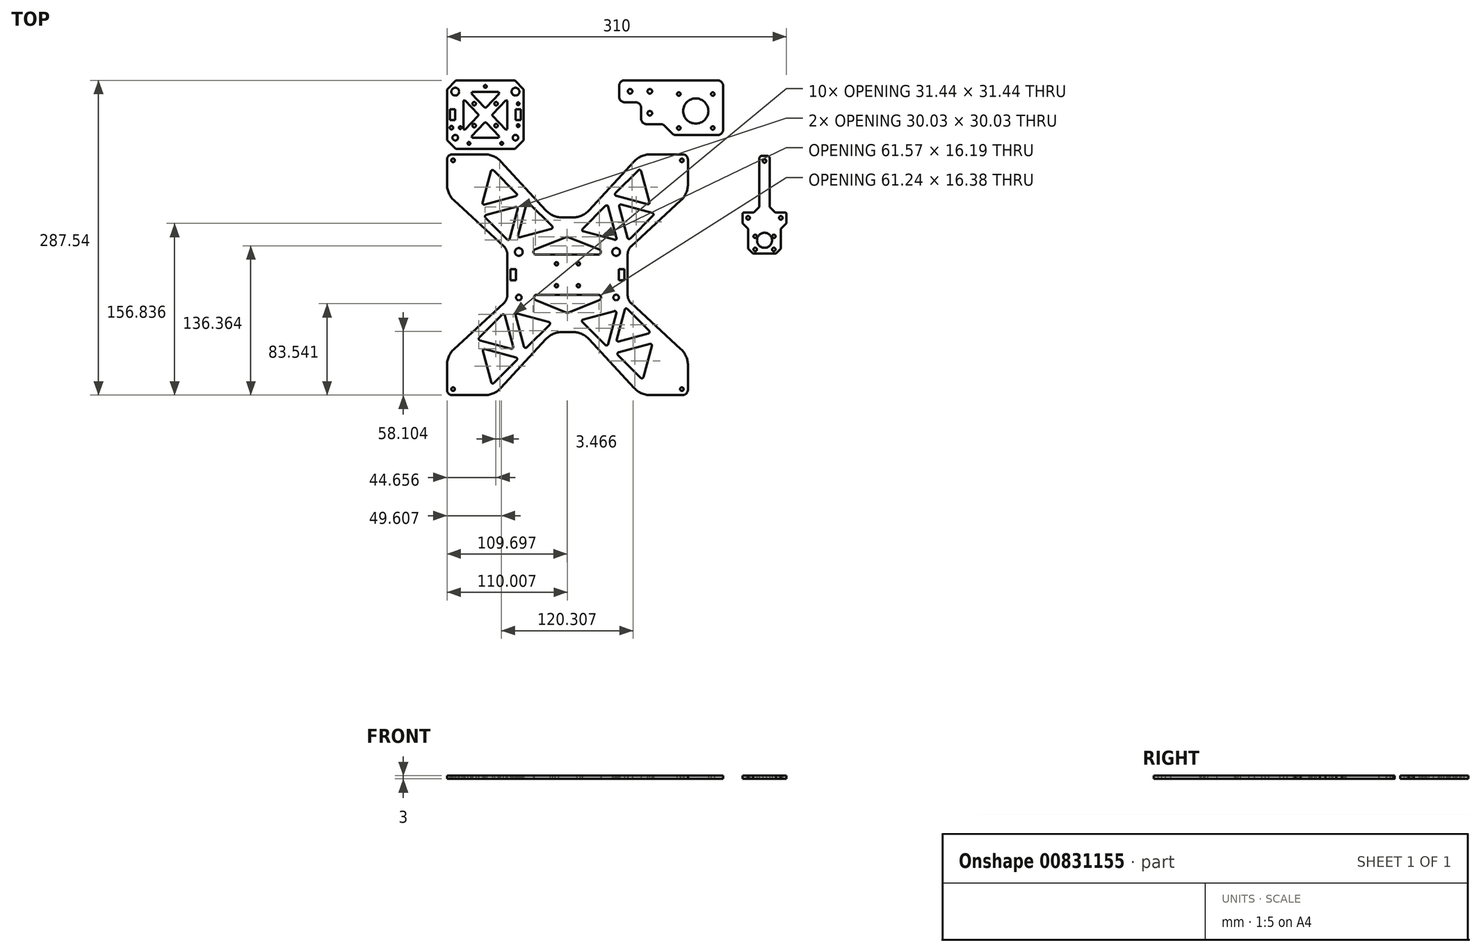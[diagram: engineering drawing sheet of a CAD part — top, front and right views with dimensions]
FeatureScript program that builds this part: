
annotation { "Feature Type Name" : "Feature", "Feature Type Description" : "" }
export const myFeature = defineFeature(function(context is Context, id is Id, definition is map)
    precondition{}
    {
        {
            var Q0;
            Q0=qCreatedBy(makeId("Top.planeOp"),FACE);
            var sketch = newSketch(context, id + "F0", { "sketchPlane" : qUnion([Q0])});
            skArc(sketch, "E0", {"start": v(205.4, 138.93) * mm, "mid": v(203.94, 142.47) * mm, "end": v(200.4, 143.93) * mm});
            skLineSegment(sketch, "E1", {"start": v(200.4, 143.93) * mm, "end": v(126.4, 143.93) * mm});
            skArc(sketch, "E2", {"start": v(126.4, 143.93) * mm, "mid": v(122.87, 142.47) * mm, "end": v(121.4, 138.93) * mm});
            skLineSegment(sketch, "E3", {"start": v(121.4, 138.93) * mm, "end": v(121.4, 107.13) * mm});
            skArc(sketch, "E4", {"start": v(121.4, 107.13) * mm, "mid": v(122.87, 103.6) * mm, "end": v(126.4, 102.13) * mm});
            skLineSegment(sketch, "E5", {"start": v(126.4, 102.13) * mm, "end": v(153.13, 102.13) * mm});
            skArc(sketch, "E6", {"start": v(156.67, 100.67) * mm, "mid": v(155.05, 101.75) * mm, "end": v(153.13, 102.13) * mm});
            skLineSegment(sketch, "E7", {"start": v(156.67, 100.67) * mm, "end": v(182.94, 74.4) * mm});
            skArc(sketch, "E8", {"start": v(184.4, 70.86) * mm, "mid": v(184.02, 72.78) * mm, "end": v(182.94, 74.4) * mm});
            skLineSegment(sketch, "E9", {"start": v(184.4, 70.86) * mm, "end": v(184.4, 46.93) * mm});
            skArc(sketch, "E10", {"start": v(184.4, 46.93) * mm, "mid": v(185.87, 43.4) * mm, "end": v(189.4, 41.93) * mm});
            skLineSegment(sketch, "E11", {"start": v(189.4, 41.93) * mm, "end": v(200.4, 41.93) * mm});
            skArc(sketch, "E12", {"start": v(200.4, 41.93) * mm, "mid": v(203.94, 43.4) * mm, "end": v(205.4, 46.93) * mm});
            skLineSegment(sketch, "E13", {"start": v(205.4, 46.93) * mm, "end": v(205.4, 138.93) * mm});
            skCircle(sketch, "E14", {"center": v(196.47, 51.76) * mm, "radius": 2.13 * mm});
            skCircle(sketch, "E15", {"center": v(196.47, 92.76) * mm, "radius": 2.13 * mm});
            skCircle(sketch, "E16", {"center": v(196.47, 134.1) * mm, "radius": 2.13 * mm});
            skArc(sketch, "E17", {"start": v(164.8, 136.93) * mm, "mid": v(166.4, 138.53) * mm, "end": v(164.8, 140.13) * mm});
            skLineSegment(sketch, "E18", {"start": v(164.8, 140.13) * mm, "end": v(158.8, 140.13) * mm});
            skArc(sketch, "E19", {"start": v(158.8, 140.13) * mm, "mid": v(157.2, 138.53) * mm, "end": v(158.8, 136.93) * mm});
            skLineSegment(sketch, "E20", {"start": v(158.8, 136.93) * mm, "end": v(164.8, 136.93) * mm});
            skArc(sketch, "E21", {"start": v(133.8, 105.93) * mm, "mid": v(135.4, 107.53) * mm, "end": v(133.8, 109.13) * mm});
            skLineSegment(sketch, "E22", {"start": v(133.8, 109.13) * mm, "end": v(127.8, 109.13) * mm});
            skArc(sketch, "E23", {"start": v(127.8, 109.13) * mm, "mid": v(126.2, 107.53) * mm, "end": v(127.8, 105.93) * mm});
            skLineSegment(sketch, "E24", {"start": v(127.8, 105.93) * mm, "end": v(133.8, 105.93) * mm});
            skArc(sketch, "E25", {"start": v(127.8, 140.13) * mm, "mid": v(126.2, 138.53) * mm, "end": v(127.8, 136.93) * mm});
            skLineSegment(sketch, "E26", {"start": v(127.8, 136.93) * mm, "end": v(133.8, 136.93) * mm});
            skArc(sketch, "E27", {"start": v(133.8, 136.93) * mm, "mid": v(135.4, 138.53) * mm, "end": v(133.8, 140.13) * mm});
            skLineSegment(sketch, "E28", {"start": v(133.8, 140.13) * mm, "end": v(127.8, 140.13) * mm});
            skLineSegment(sketch, "E29", {"start": v(149.1, 134.53) * mm, "end": v(143.1, 134.53) * mm});
            skArc(sketch, "E30", {"start": v(143.1, 134.53) * mm, "mid": v(131.6, 123.03) * mm, "end": v(143.1, 111.53) * mm});
            skLineSegment(sketch, "E31", {"start": v(143.1, 111.53) * mm, "end": v(149.1, 111.53) * mm});
            skArc(sketch, "E32", {"start": v(149.1, 111.53) * mm, "mid": v(160.6, 123.03) * mm, "end": v(149.1, 134.53) * mm});
            skArc(sketch, "E33", {"start": v(164.8, 105.93) * mm, "mid": v(166.4, 107.53) * mm, "end": v(164.8, 109.13) * mm});
            skLineSegment(sketch, "E34", {"start": v(164.8, 109.13) * mm, "end": v(158.8, 109.13) * mm});
            skArc(sketch, "E35", {"start": v(158.8, 109.13) * mm, "mid": v(157.2, 107.53) * mm, "end": v(158.8, 105.93) * mm});
            skLineSegment(sketch, "E36", {"start": v(158.8, 105.93) * mm, "end": v(164.8, 105.93) * mm});
            skLineSegment(sketch, "E37", {"start": v(205.25, -63.38) * mm, "end": v(205.25, -1.88) * mm});
            skArc(sketch, "E38", {"start": v(205.25, -1.88) * mm, "mid": v(204.37, 0.24) * mm, "end": v(202.25, 1.12) * mm});
            skLineSegment(sketch, "E39", {"start": v(202.25, 1.12) * mm, "end": v(168.25, 1.12) * mm});
            skArc(sketch, "E40", {"start": v(168.25, 1.12) * mm, "mid": v(166.12, 0.24) * mm, "end": v(165.25, -1.88) * mm});
            skLineSegment(sketch, "E41", {"start": v(165.25, -1.88) * mm, "end": v(165.25, -43.38) * mm});
            skArc(sketch, "E42", {"start": v(162.25, -46.38) * mm, "mid": v(164.37, -45.5) * mm, "end": v(165.25, -43.38) * mm});
            skLineSegment(sketch, "E43", {"start": v(162.25, -46.38) * mm, "end": v(120.75, -46.28) * mm});
            skArc(sketch, "E44", {"start": v(120.75, -46.28) * mm, "mid": v(118.63, -47.16) * mm, "end": v(117.75, -49.28) * mm});
            skLineSegment(sketch, "E45", {"start": v(117.75, -49.28) * mm, "end": v(117.75, -63.38) * mm});
            skArc(sketch, "E46", {"start": v(117.75, -63.38) * mm, "mid": v(118.62, -65.5) * mm, "end": v(120.75, -66.38) * mm});
            skLineSegment(sketch, "E47", {"start": v(120.75, -66.38) * mm, "end": v(202.25, -66.38) * mm});
            skArc(sketch, "E48", {"start": v(202.25, -66.38) * mm, "mid": v(204.37, -65.5) * mm, "end": v(205.25, -63.38) * mm});
            skCircle(sketch, "E49", {"center": v(195.25, -28.88) * mm, "radius": 2.15 * mm});
            skCircle(sketch, "E50", {"center": v(175.25, -28.88) * mm, "radius": 2.15 * mm});
            skCircle(sketch, "E51", {"center": v(195.25, -8.88) * mm, "radius": 2.15 * mm});
            skCircle(sketch, "E52", {"center": v(127.75, -56.33) * mm, "radius": 2.15 * mm});
            skCircle(sketch, "E53", {"center": v(147.75, -56.33) * mm, "radius": 2.15 * mm});
            skCircle(sketch, "E54", {"center": v(175.25, -8.88) * mm, "radius": 2.15 * mm});
            skLineSegment(sketch, "E55", {"start": v(117.74, -126.84) * mm, "end": v(117.74, -140.93) * mm});
            skArc(sketch, "E56", {"start": v(117.74, -140.93) * mm, "mid": v(118.62, -143.05) * mm, "end": v(120.74, -143.93) * mm});
            skLineSegment(sketch, "E57", {"start": v(120.74, -143.93) * mm, "end": v(202.24, -143.93) * mm});
            skArc(sketch, "E58", {"start": v(202.24, -143.93) * mm, "mid": v(204.37, -143.05) * mm, "end": v(205.24, -140.93) * mm});
            skLineSegment(sketch, "E59", {"start": v(205.24, -140.93) * mm, "end": v(205.24, -79.43) * mm});
            skArc(sketch, "E60", {"start": v(205.24, -79.43) * mm, "mid": v(204.37, -77.31) * mm, "end": v(202.24, -76.43) * mm});
            skLineSegment(sketch, "E61", {"start": v(202.24, -76.43) * mm, "end": v(168.24, -76.43) * mm});
            skArc(sketch, "E62", {"start": v(168.24, -76.43) * mm, "mid": v(166.12, -77.31) * mm, "end": v(165.24, -79.43) * mm});
            skLineSegment(sketch, "E63", {"start": v(165.24, -79.43) * mm, "end": v(165.24, -120.93) * mm});
            skArc(sketch, "E64", {"start": v(162.24, -123.93) * mm, "mid": v(164.37, -123.05) * mm, "end": v(165.24, -120.93) * mm});
            skLineSegment(sketch, "E65", {"start": v(162.24, -123.93) * mm, "end": v(120.75, -123.84) * mm});
            skArc(sketch, "E66", {"start": v(120.75, -123.84) * mm, "mid": v(118.63, -124.71) * mm, "end": v(117.74, -126.84) * mm});
            skCircle(sketch, "E67", {"center": v(127.74, -133.89) * mm, "radius": 2.15 * mm});
            skCircle(sketch, "E68", {"center": v(147.74, -133.89) * mm, "radius": 2.15 * mm});
            skCircle(sketch, "E69", {"center": v(175.24, -106.43) * mm, "radius": 2.15 * mm});
            skCircle(sketch, "E70", {"center": v(195.24, -106.43) * mm, "radius": 2.15 * mm});
            skCircle(sketch, "E71", {"center": v(175.24, -86.43) * mm, "radius": 2.15 * mm});
            skCircle(sketch, "E72", {"center": v(195.24, -86.43) * mm, "radius": 2.15 * mm});
            skLineSegment(sketch, "E73", {"start": v(134.6, 23.18) * mm, "end": v(134.6, -38.32) * mm});
            skArc(sketch, "E74", {"start": v(134.6, -38.32) * mm, "mid": v(135.47, -40.44) * mm, "end": v(137.6, -41.32) * mm});
            skLineSegment(sketch, "E75", {"start": v(137.6, -41.32) * mm, "end": v(151.6, -41.32) * mm});
            skArc(sketch, "E76", {"start": v(151.6, -41.32) * mm, "mid": v(153.72, -40.44) * mm, "end": v(154.6, -38.32) * mm});
            skLineSegment(sketch, "E77", {"start": v(154.6, -38.32) * mm, "end": v(154.6, 3.18) * mm});
            skArc(sketch, "E78", {"start": v(157.6, 6.18) * mm, "mid": v(155.47, 5.3) * mm, "end": v(154.6, 3.18) * mm});
            skLineSegment(sketch, "E79", {"start": v(157.6, 6.18) * mm, "end": v(199.1, 6.18) * mm});
            skArc(sketch, "E80", {"start": v(199.1, 6.18) * mm, "mid": v(201.22, 7.06) * mm, "end": v(202.1, 9.18) * mm});
            skLineSegment(sketch, "E81", {"start": v(202.1, 9.18) * mm, "end": v(202.1, 23.18) * mm});
            skArc(sketch, "E82", {"start": v(202.1, 23.18) * mm, "mid": v(201.22, 25.3) * mm, "end": v(199.1, 26.18) * mm});
            skLineSegment(sketch, "E83", {"start": v(199.1, 26.18) * mm, "end": v(137.6, 26.18) * mm});
            skArc(sketch, "E84", {"start": v(137.6, 26.18) * mm, "mid": v(135.47, 25.3) * mm, "end": v(134.6, 23.18) * mm});
            skCircle(sketch, "E85", {"center": v(144.6, -31.32) * mm, "radius": 2.15 * mm});
            skCircle(sketch, "E86", {"center": v(192.1, 16.18) * mm, "radius": 2.15 * mm});
            skCircle(sketch, "E87", {"center": v(172.1, 16.18) * mm, "radius": 2.15 * mm});
            skCircle(sketch, "E88", {"center": v(144.6, -11.32) * mm, "radius": 2.15 * mm});
            skArc(sketch, "E89", {"start": v(94.35, 38.03) * mm, "mid": v(95.81, 34.5) * mm, "end": v(99.35, 33.03) * mm});
            skLineSegment(sketch, "E90", {"start": v(99.35, 33.03) * mm, "end": v(173.35, 33.03) * mm});
            skArc(sketch, "E91", {"start": v(173.35, 33.03) * mm, "mid": v(176.88, 34.5) * mm, "end": v(178.35, 38.03) * mm});
            skLineSegment(sketch, "E92", {"start": v(178.35, 38.03) * mm, "end": v(178.35, 69.83) * mm});
            skArc(sketch, "E93", {"start": v(178.35, 69.83) * mm, "mid": v(176.88, 73.37) * mm, "end": v(173.35, 74.83) * mm});
            skLineSegment(sketch, "E94", {"start": v(173.35, 74.83) * mm, "end": v(146.62, 74.83) * mm});
            skArc(sketch, "E95", {"start": v(143.08, 76.3) * mm, "mid": v(144.7, 75.21) * mm, "end": v(146.62, 74.83) * mm});
            skLineSegment(sketch, "E96", {"start": v(143.08, 76.3) * mm, "end": v(116.8, 102.57) * mm});
            skArc(sketch, "E97", {"start": v(115.35, 106.1) * mm, "mid": v(115.73, 104.19) * mm, "end": v(116.8, 102.57) * mm});
            skLineSegment(sketch, "E98", {"start": v(115.35, 106.1) * mm, "end": v(115.35, 130.03) * mm});
            skArc(sketch, "E99", {"start": v(115.35, 130.03) * mm, "mid": v(113.88, 133.57) * mm, "end": v(110.35, 135.03) * mm});
            skLineSegment(sketch, "E100", {"start": v(110.35, 135.03) * mm, "end": v(99.35, 135.03) * mm});
            skArc(sketch, "E101", {"start": v(99.35, 135.03) * mm, "mid": v(95.81, 133.57) * mm, "end": v(94.35, 130.03) * mm});
            skLineSegment(sketch, "E102", {"start": v(94.35, 130.03) * mm, "end": v(94.35, 38.03) * mm});
            skCircle(sketch, "E103", {"center": v(103.28, 125.2) * mm, "radius": 2.13 * mm});
            skCircle(sketch, "E104", {"center": v(103.28, 84.2) * mm, "radius": 2.13 * mm});
            skCircle(sketch, "E105", {"center": v(103.28, 42.86) * mm, "radius": 2.13 * mm});
            skArc(sketch, "E106", {"start": v(165.95, 71.03) * mm, "mid": v(164.35, 69.43) * mm, "end": v(165.95, 67.83) * mm});
            skLineSegment(sketch, "E107", {"start": v(165.95, 67.83) * mm, "end": v(171.95, 67.83) * mm});
            skArc(sketch, "E108", {"start": v(171.95, 67.83) * mm, "mid": v(173.55, 69.43) * mm, "end": v(171.95, 71.03) * mm});
            skLineSegment(sketch, "E109", {"start": v(171.95, 71.03) * mm, "end": v(165.95, 71.03) * mm});
            skArc(sketch, "E110", {"start": v(171.95, 36.83) * mm, "mid": v(173.55, 38.43) * mm, "end": v(171.95, 40.03) * mm});
            skLineSegment(sketch, "E111", {"start": v(171.95, 40.03) * mm, "end": v(165.95, 40.03) * mm});
            skArc(sketch, "E112", {"start": v(165.95, 40.03) * mm, "mid": v(164.35, 38.43) * mm, "end": v(165.95, 36.83) * mm});
            skLineSegment(sketch, "E113", {"start": v(165.95, 36.83) * mm, "end": v(171.95, 36.83) * mm});
            skLineSegment(sketch, "E114", {"start": v(150.65, 42.43) * mm, "end": v(156.65, 42.43) * mm});
            skArc(sketch, "E115", {"start": v(156.65, 42.43) * mm, "mid": v(168.15, 53.93) * mm, "end": v(156.65, 65.43) * mm});
            skLineSegment(sketch, "E116", {"start": v(156.65, 65.43) * mm, "end": v(150.65, 65.43) * mm});
            skArc(sketch, "E117", {"start": v(150.65, 65.43) * mm, "mid": v(139.15, 53.93) * mm, "end": v(150.65, 42.43) * mm});
            skArc(sketch, "E118", {"start": v(134.95, 40.03) * mm, "mid": v(133.35, 38.43) * mm, "end": v(134.95, 36.83) * mm});
            skLineSegment(sketch, "E119", {"start": v(134.95, 36.83) * mm, "end": v(140.95, 36.83) * mm});
            skArc(sketch, "E120", {"start": v(140.95, 36.83) * mm, "mid": v(142.55, 38.43) * mm, "end": v(140.95, 40.03) * mm});
            skLineSegment(sketch, "E121", {"start": v(140.95, 40.03) * mm, "end": v(134.95, 40.03) * mm});
            skArc(sketch, "E122", {"start": v(134.95, 71.03) * mm, "mid": v(133.35, 69.43) * mm, "end": v(134.95, 67.83) * mm});
            skLineSegment(sketch, "E123", {"start": v(134.95, 67.83) * mm, "end": v(140.95, 67.83) * mm});
            skArc(sketch, "E124", {"start": v(140.95, 67.83) * mm, "mid": v(142.55, 69.43) * mm, "end": v(140.95, 71.03) * mm});
            skLineSegment(sketch, "E125", {"start": v(140.95, 71.03) * mm, "end": v(134.95, 71.03) * mm});
            skLineSegment(sketch, "E126", {"start": v(59.22, -44.47) * mm, "end": v(27.33, -44.47) * mm});
            skArc(sketch, "E127", {"start": v(27.33, -44.47) * mm, "mid": v(23.8, -45.93) * mm, "end": v(22.33, -49.47) * mm});
            skLineSegment(sketch, "E128", {"start": v(22.33, -49.47) * mm, "end": v(22.33, -138.36) * mm});
            skArc(sketch, "E129", {"start": v(22.33, -138.36) * mm, "mid": v(23.8, -141.9) * mm, "end": v(27.33, -143.36) * mm});
            skLineSegment(sketch, "E130", {"start": v(27.33, -143.36) * mm, "end": v(99.71, -143.36) * mm});
            skArc(sketch, "E131", {"start": v(99.71, -143.36) * mm, "mid": v(103.25, -141.9) * mm, "end": v(104.71, -138.36) * mm});
            skLineSegment(sketch, "E132", {"start": v(104.71, -138.36) * mm, "end": v(104.71, -134.17) * mm});
            skArc(sketch, "E133", {"start": v(106.57, -129.68) * mm, "mid": v(105.2, -131.74) * mm, "end": v(104.71, -134.17) * mm});
            skLineSegment(sketch, "E134", {"start": v(106.57, -129.68) * mm, "end": v(115.55, -120.7) * mm});
            skArc(sketch, "E135", {"start": v(120.04, -118.84) * mm, "mid": v(117.61, -119.32) * mm, "end": v(115.55, -120.7) * mm});
            skLineSegment(sketch, "E136", {"start": v(120.04, -118.84) * mm, "end": v(149.78, -118.84) * mm});
            skArc(sketch, "E137", {"start": v(149.78, -118.84) * mm, "mid": v(153.32, -117.37) * mm, "end": v(154.78, -113.84) * mm});
            skLineSegment(sketch, "E138", {"start": v(154.78, -113.84) * mm, "end": v(154.78, -76.38) * mm});
            skArc(sketch, "E139", {"start": v(154.78, -76.38) * mm, "mid": v(153.32, -72.84) * mm, "end": v(149.78, -71.38) * mm});
            skLineSegment(sketch, "E140", {"start": v(149.78, -71.38) * mm, "end": v(120.04, -71.38) * mm});
            skArc(sketch, "E141", {"start": v(115.55, -69.52) * mm, "mid": v(117.61, -70.9) * mm, "end": v(120.04, -71.38) * mm});
            skLineSegment(sketch, "E142", {"start": v(115.55, -69.52) * mm, "end": v(106.57, -60.54) * mm});
            skArc(sketch, "E143", {"start": v(104.71, -56.05) * mm, "mid": v(105.2, -58.48) * mm, "end": v(106.57, -60.54) * mm});
            skLineSegment(sketch, "E144", {"start": v(104.71, -56.05) * mm, "end": v(104.71, -49.47) * mm});
            skArc(sketch, "E145", {"start": v(104.71, -49.47) * mm, "mid": v(103.25, -45.93) * mm, "end": v(99.71, -44.47) * mm});
            skLineSegment(sketch, "E146", {"start": v(99.71, -44.47) * mm, "end": v(67.83, -44.47) * mm});
            skArc(sketch, "E147", {"start": v(67.83, -44.47) * mm, "mid": v(67.06, -44.62) * mm, "end": v(66.42, -45.06) * mm});
            skLineSegment(sketch, "E148", {"start": v(66.42, -45.06) * mm, "end": v(64.94, -46.53) * mm});
            skArc(sketch, "E149", {"start": v(62.1, -46.53) * mm, "mid": v(63.52, -47.12) * mm, "end": v(64.94, -46.53) * mm});
            skLineSegment(sketch, "E150", {"start": v(62.1, -46.53) * mm, "end": v(60.63, -45.06) * mm});
            skArc(sketch, "E151", {"start": v(60.63, -45.06) * mm, "mid": v(59.98, -44.62) * mm, "end": v(59.22, -44.47) * mm});
            skCircle(sketch, "E152", {"center": v(94.46, -54.47) * mm, "radius": 3.56 * mm});
            skCircle(sketch, "E153", {"center": v(94.46, -133.36) * mm, "radius": 3.56 * mm});
            skCircle(sketch, "E154", {"center": v(32.59, -54.47) * mm, "radius": 2.55 * mm});
            skCircle(sketch, "E155", {"center": v(32.59, -133.36) * mm, "radius": 2.55 * mm});
            skCircle(sketch, "E156", {"center": v(89.52, -98.83) * mm, "radius": 2.1 * mm});
            skCircle(sketch, "E157", {"center": v(37.52, -98.83) * mm, "radius": 2.1 * mm});
            skCircle(sketch, "E158", {"center": v(89.52, -78.83) * mm, "radius": 2.1 * mm});
            skCircle(sketch, "E159", {"center": v(37.52, -78.83) * mm, "radius": 2.1 * mm});
            skCircle(sketch, "E160", {"center": v(145.28, -111.34) * mm, "radius": 1.6 * mm});
            skCircle(sketch, "E161", {"center": v(129.78, -95.84) * mm, "radius": 11.5 * mm});
            skCircle(sketch, "E162", {"center": v(145.28, -80.34) * mm, "radius": 1.6 * mm});
            skCircle(sketch, "E163", {"center": v(114.28, -111.34) * mm, "radius": 1.6 * mm});
            skCircle(sketch, "E164", {"center": v(114.28, -80.34) * mm, "radius": 1.6 * mm});
            skArc(sketch, "E165", {"start": v(47.67, -58.84) * mm, "mid": v(44.84, -60.01) * mm, "end": v(43.67, -62.84) * mm});
            skLineSegment(sketch, "E166", {"start": v(43.67, -62.84) * mm, "end": v(43.67, -123.72) * mm});
            skArc(sketch, "E167", {"start": v(43.67, -123.72) * mm, "mid": v(44.84, -126.54) * mm, "end": v(47.67, -127.72) * mm});
            skLineSegment(sketch, "E168", {"start": v(47.67, -127.72) * mm, "end": v(79.38, -127.72) * mm});
            skArc(sketch, "E169", {"start": v(79.38, -127.72) * mm, "mid": v(82.2, -126.54) * mm, "end": v(83.38, -123.72) * mm});
            skLineSegment(sketch, "E170", {"start": v(83.38, -123.72) * mm, "end": v(83.38, -62.84) * mm});
            skArc(sketch, "E171", {"start": v(83.38, -62.84) * mm, "mid": v(82.2, -60.01) * mm, "end": v(79.38, -58.84) * mm});
            skLineSegment(sketch, "E172", {"start": v(79.38, -58.84) * mm, "end": v(47.67, -58.84) * mm});
            skLineSegment(sketch, "E173", {"start": v(62.1, -22.47) * mm, "end": v(62.1, -36.47) * mm});
            skArc(sketch, "E174", {"start": v(62.1, -36.47) * mm, "mid": v(62.97, -38.6) * mm, "end": v(65.1, -39.47) * mm});
            skLineSegment(sketch, "E175", {"start": v(65.1, -39.47) * mm, "end": v(126.6, -39.47) * mm});
            skArc(sketch, "E176", {"start": v(126.6, -39.47) * mm, "mid": v(128.72, -38.6) * mm, "end": v(129.6, -36.47) * mm});
            skLineSegment(sketch, "E177", {"start": v(129.6, -36.47) * mm, "end": v(129.6, 25.03) * mm});
            skArc(sketch, "E178", {"start": v(129.6, 25.03) * mm, "mid": v(128.72, 27.15) * mm, "end": v(126.6, 28.03) * mm});
            skLineSegment(sketch, "E179", {"start": v(126.6, 28.03) * mm, "end": v(112.6, 28.03) * mm});
            skArc(sketch, "E180", {"start": v(112.6, 28.03) * mm, "mid": v(110.47, 27.15) * mm, "end": v(109.6, 25.03) * mm});
            skLineSegment(sketch, "E181", {"start": v(109.6, 25.03) * mm, "end": v(109.6, -16.47) * mm});
            skArc(sketch, "E182", {"start": v(106.6, -19.47) * mm, "mid": v(108.72, -18.6) * mm, "end": v(109.6, -16.47) * mm});
            skLineSegment(sketch, "E183", {"start": v(106.6, -19.47) * mm, "end": v(65.1, -19.47) * mm});
            skArc(sketch, "E184", {"start": v(65.1, -19.47) * mm, "mid": v(62.97, -20.35) * mm, "end": v(62.1, -22.47) * mm});
            skCircle(sketch, "E185", {"center": v(72.1, -29.47) * mm, "radius": 2.15 * mm});
            skCircle(sketch, "E186", {"center": v(92.1, -29.47) * mm, "radius": 2.15 * mm});
            skCircle(sketch, "E187", {"center": v(119.6, 18.03) * mm, "radius": 2.15 * mm});
            skCircle(sketch, "E188", {"center": v(119.6, -1.97) * mm, "radius": 2.15 * mm});
            skLineSegment(sketch, "E189", {"start": v(79.85, 72.21) * mm, "end": v(79.85, 28.05) * mm});
            skLineSegment(sketch, "E190", {"start": v(79.85, 28.05) * mm, "end": v(74.77, 22.97) * mm});
            skLineSegment(sketch, "E191", {"start": v(74.77, 22.97) * mm, "end": v(65.87, 22.97) * mm});
            skArc(sketch, "E192", {"start": v(65.87, 22.97) * mm, "mid": v(64.97, 22.6) * mm, "end": v(64.6, 21.7) * mm});
            skLineSegment(sketch, "E193", {"start": v(64.6, 21.7) * mm, "end": v(64.6, 13.03) * mm});
            skLineSegment(sketch, "E194", {"start": v(64.6, 13.03) * mm, "end": v(69.6, 8.03) * mm});
            skLineSegment(sketch, "E195", {"start": v(69.6, 8.03) * mm, "end": v(69.6, -9.97) * mm});
            skLineSegment(sketch, "E196", {"start": v(69.6, -9.97) * mm, "end": v(74.1, -14.47) * mm});
            skLineSegment(sketch, "E197", {"start": v(74.1, -14.47) * mm, "end": v(95.1, -14.47) * mm});
            skLineSegment(sketch, "E198", {"start": v(95.1, -14.47) * mm, "end": v(99.6, -9.97) * mm});
            skLineSegment(sketch, "E199", {"start": v(99.6, -9.97) * mm, "end": v(99.6, 8.03) * mm});
            skLineSegment(sketch, "E200", {"start": v(99.6, 8.03) * mm, "end": v(104.6, 13.03) * mm});
            skLineSegment(sketch, "E201", {"start": v(104.6, 13.03) * mm, "end": v(104.6, 21.7) * mm});
            skArc(sketch, "E202", {"start": v(104.6, 21.7) * mm, "mid": v(104.22, 22.6) * mm, "end": v(103.33, 22.97) * mm});
            skLineSegment(sketch, "E203", {"start": v(103.33, 22.97) * mm, "end": v(94.43, 22.97) * mm});
            skLineSegment(sketch, "E204", {"start": v(94.43, 22.97) * mm, "end": v(89.35, 28.05) * mm});
            skLineSegment(sketch, "E205", {"start": v(89.35, 28.05) * mm, "end": v(89.35, 72.21) * mm});
            skArc(sketch, "E206", {"start": v(89.35, 72.21) * mm, "mid": v(88.6, 74) * mm, "end": v(86.8, 74.75) * mm});
            skLineSegment(sketch, "E207", {"start": v(86.8, 74.75) * mm, "end": v(82.39, 74.75) * mm});
            skArc(sketch, "E208", {"start": v(82.39, 74.75) * mm, "mid": v(80.6, 74) * mm, "end": v(79.85, 72.21) * mm});
            skCircle(sketch, "E209", {"center": v(84.6, -2.47) * mm, "radius": 6.88 * mm});
            skCircle(sketch, "E210", {"center": v(76.1, 1.13) * mm, "radius": 1.59 * mm});
            skCircle(sketch, "E211", {"center": v(93.1, 1.13) * mm, "radius": 1.59 * mm});
            skCircle(sketch, "E212", {"center": v(76.1, -10.87) * mm, "radius": 1.59 * mm});
            skCircle(sketch, "E213", {"center": v(93.1, -10.87) * mm, "radius": 1.59 * mm});
            skCircle(sketch, "E214", {"center": v(84.6, 69.99) * mm, "radius": 1.64 * mm});
            skCircle(sketch, "E215", {"center": v(99.51, 18) * mm, "radius": 1.64 * mm});
            skCircle(sketch, "E216", {"center": v(69.57, 18) * mm, "radius": 1.64 * mm});
            skLineSegment(sketch, "E217", {"start": v(74.1, 32.84) * mm, "end": v(74.1, 77) * mm});
            skLineSegment(sketch, "E218", {"start": v(74.1, 77) * mm, "end": v(79.18, 82.08) * mm});
            skLineSegment(sketch, "E219", {"start": v(79.18, 82.08) * mm, "end": v(88.08, 82.08) * mm});
            skArc(sketch, "E220", {"start": v(88.08, 82.08) * mm, "mid": v(88.97, 82.45) * mm, "end": v(89.35, 83.35) * mm});
            skLineSegment(sketch, "E221", {"start": v(89.35, 83.35) * mm, "end": v(89.35, 92.02) * mm});
            skLineSegment(sketch, "E222", {"start": v(89.35, 92.02) * mm, "end": v(84.35, 97.02) * mm});
            skLineSegment(sketch, "E223", {"start": v(84.35, 97.02) * mm, "end": v(84.35, 116.52) * mm});
            skLineSegment(sketch, "E224", {"start": v(84.35, 116.52) * mm, "end": v(76.35, 124.52) * mm});
            skLineSegment(sketch, "E225", {"start": v(76.35, 124.52) * mm, "end": v(62.35, 124.52) * mm});
            skLineSegment(sketch, "E226", {"start": v(62.35, 124.52) * mm, "end": v(54.35, 116.52) * mm});
            skLineSegment(sketch, "E227", {"start": v(54.35, 116.52) * mm, "end": v(54.35, 97.02) * mm});
            skLineSegment(sketch, "E228", {"start": v(54.35, 97.02) * mm, "end": v(49.35, 92.02) * mm});
            skLineSegment(sketch, "E229", {"start": v(49.35, 92.02) * mm, "end": v(49.35, 83.35) * mm});
            skArc(sketch, "E230", {"start": v(49.35, 83.35) * mm, "mid": v(49.72, 82.45) * mm, "end": v(50.62, 82.08) * mm});
            skLineSegment(sketch, "E231", {"start": v(50.62, 82.08) * mm, "end": v(59.52, 82.08) * mm});
            skLineSegment(sketch, "E232", {"start": v(59.52, 82.08) * mm, "end": v(64.6, 77) * mm});
            skLineSegment(sketch, "E233", {"start": v(64.6, 77) * mm, "end": v(64.6, 32.84) * mm});
            skArc(sketch, "E234", {"start": v(64.6, 32.84) * mm, "mid": v(65.34, 31.04) * mm, "end": v(67.14, 30.3) * mm});
            skLineSegment(sketch, "E235", {"start": v(67.14, 30.3) * mm, "end": v(71.56, 30.3) * mm});
            skArc(sketch, "E236", {"start": v(71.56, 30.3) * mm, "mid": v(73.35, 31.04) * mm, "end": v(74.1, 32.84) * mm});
            skCircle(sketch, "E237", {"center": v(69.35, 120.08) * mm, "radius": 1.24 * mm});
            skCircle(sketch, "E238", {"center": v(74.35, 95.02) * mm, "radius": 1.6 * mm});
            skCircle(sketch, "E239", {"center": v(69.35, 107.52) * mm, "radius": 8.1 * mm});
            skCircle(sketch, "E240", {"center": v(64.35, 94.98) * mm, "radius": 1.6 * mm});
            skCircle(sketch, "E241", {"center": v(69.35, 35.06) * mm, "radius": 1.64 * mm});
            skCircle(sketch, "E242", {"center": v(84.38, 87.05) * mm, "radius": 1.64 * mm});
            skCircle(sketch, "E243", {"center": v(54.43, 87.05) * mm, "radius": 1.64 * mm});
            skLineSegment(sketch, "E244", {"start": v(48.67, -111.25) * mm, "end": v(48.67, -119.28) * mm});
            skArc(sketch, "E245", {"start": v(48.67, -119.28) * mm, "mid": v(48.72, -119.52) * mm, "end": v(48.85, -119.73) * mm});
            skLineSegment(sketch, "E246", {"start": v(48.85, -119.73) * mm, "end": v(51.66, -122.53) * mm});
            skArc(sketch, "E247", {"start": v(51.66, -122.53) * mm, "mid": v(51.86, -122.67) * mm, "end": v(52.1, -122.72) * mm});
            skLineSegment(sketch, "E248", {"start": v(52.1, -122.72) * mm, "end": v(73.17, -122.72) * mm});
            skArc(sketch, "E249", {"start": v(73.17, -122.72) * mm, "mid": v(73.42, -122.67) * mm, "end": v(73.62, -122.53) * mm});
            skLineSegment(sketch, "E250", {"start": v(73.62, -122.53) * mm, "end": v(76.42, -119.73) * mm});
            skArc(sketch, "E251", {"start": v(76.42, -119.73) * mm, "mid": v(76.56, -119.52) * mm, "end": v(76.61, -119.28) * mm});
            skLineSegment(sketch, "E252", {"start": v(76.61, -119.28) * mm, "end": v(76.61, -111.25) * mm});
            skArc(sketch, "E253", {"start": v(76.61, -111.25) * mm, "mid": v(76.56, -111) * mm, "end": v(76.42, -110.8) * mm});
            skLineSegment(sketch, "E254", {"start": v(76.42, -110.8) * mm, "end": v(73.62, -108) * mm});
            skArc(sketch, "E255", {"start": v(73.62, -108) * mm, "mid": v(73.42, -107.86) * mm, "end": v(73.17, -107.8) * mm});
            skLineSegment(sketch, "E256", {"start": v(73.17, -107.8) * mm, "end": v(52.1, -107.8) * mm});
            skArc(sketch, "E257", {"start": v(52.1, -107.8) * mm, "mid": v(51.86, -107.86) * mm, "end": v(51.66, -108) * mm});
            skLineSegment(sketch, "E258", {"start": v(51.66, -108) * mm, "end": v(48.85, -110.8) * mm});
            skArc(sketch, "E259", {"start": v(48.85, -110.8) * mm, "mid": v(48.72, -111) * mm, "end": v(48.67, -111.25) * mm});
            skCircle(sketch, "E260", {"center": v(52.69, -112.72) * mm, "radius": 1.65 * mm});
            skCircle(sketch, "E261", {"center": v(72.69, -112.72) * mm, "radius": 1.65 * mm});
            skLineSegment(sketch, "E262", {"start": v(18.13, 35.62) * mm, "end": v(11.06, 28.54) * mm});
            skArc(sketch, "E263", {"start": v(11.06, 28.54) * mm, "mid": v(9.98, 26.92) * mm, "end": v(9.6, 25) * mm});
            skLineSegment(sketch, "E264", {"start": v(9.6, 25) * mm, "end": v(9.6, 2.08) * mm});
            skArc(sketch, "E265", {"start": v(9.6, 2.08) * mm, "mid": v(11.06, -1.46) * mm, "end": v(14.6, -2.92) * mm});
            skLineSegment(sketch, "E266", {"start": v(14.6, -2.92) * mm, "end": v(54.6, -2.92) * mm});
            skArc(sketch, "E267", {"start": v(54.6, -2.92) * mm, "mid": v(58.13, -1.46) * mm, "end": v(59.6, 2.08) * mm});
            skLineSegment(sketch, "E268", {"start": v(59.6, 2.08) * mm, "end": v(59.6, 72.08) * mm});
            skArc(sketch, "E269", {"start": v(59.6, 72.08) * mm, "mid": v(58.13, 75.62) * mm, "end": v(54.6, 77.08) * mm});
            skLineSegment(sketch, "E270", {"start": v(54.6, 77.08) * mm, "end": v(44.6, 77.08) * mm});
            skArc(sketch, "E271", {"start": v(44.6, 77.08) * mm, "mid": v(41.06, 75.62) * mm, "end": v(39.6, 72.08) * mm});
            skLineSegment(sketch, "E272", {"start": v(39.6, 72.08) * mm, "end": v(39.6, 62.08) * mm});
            skArc(sketch, "E273", {"start": v(34.6, 57.08) * mm, "mid": v(38.13, 58.54) * mm, "end": v(39.6, 62.08) * mm});
            skLineSegment(sketch, "E274", {"start": v(34.6, 57.08) * mm, "end": v(24.6, 57.08) * mm});
            skArc(sketch, "E275", {"start": v(24.6, 57.08) * mm, "mid": v(21.06, 55.62) * mm, "end": v(19.6, 52.08) * mm});
            skLineSegment(sketch, "E276", {"start": v(19.6, 52.08) * mm, "end": v(19.6, 39.15) * mm});
            skArc(sketch, "E277", {"start": v(18.13, 35.62) * mm, "mid": v(19.22, 37.24) * mm, "end": v(19.6, 39.15) * mm});
            skCircle(sketch, "E278", {"center": v(49.6, 67.08) * mm, "radius": 2.1 * mm});
            skCircle(sketch, "E279", {"center": v(31.6, 22.08) * mm, "radius": 2.6 * mm});
            skCircle(sketch, "E280", {"center": v(49.6, 39.08) * mm, "radius": 2.1 * mm});
            skCircle(sketch, "E281", {"center": v(29.6, 39.08) * mm, "radius": 2.1 * mm});
            skCircle(sketch, "E282", {"center": v(16.6, 7.08) * mm, "radius": 2.6 * mm});
            skLineSegment(sketch, "E283", {"start": v(46.8, 98.61) * mm, "end": v(46.8, 138.61) * mm});
            skArc(sketch, "E284", {"start": v(46.8, 138.61) * mm, "mid": v(45.33, 142.15) * mm, "end": v(41.8, 143.61) * mm});
            skLineSegment(sketch, "E285", {"start": v(41.8, 143.61) * mm, "end": v(-43.2, 143.61) * mm});
            skArc(sketch, "E286", {"start": v(-43.2, 143.61) * mm, "mid": v(-46.74, 142.15) * mm, "end": v(-48.2, 138.61) * mm});
            skLineSegment(sketch, "E287", {"start": v(-48.2, 138.61) * mm, "end": v(-48.2, 128.61) * mm});
            skArc(sketch, "E288", {"start": v(-48.2, 128.61) * mm, "mid": v(-46.74, 125.08) * mm, "end": v(-43.2, 123.61) * mm});
            skLineSegment(sketch, "E289", {"start": v(-43.2, 123.61) * mm, "end": v(-33.2, 123.61) * mm});
            skArc(sketch, "E290", {"start": v(-28.2, 118.61) * mm, "mid": v(-29.67, 122.15) * mm, "end": v(-33.2, 123.61) * mm});
            skLineSegment(sketch, "E291", {"start": v(-28.2, 118.61) * mm, "end": v(-28.2, 108.61) * mm});
            skArc(sketch, "E292", {"start": v(-28.2, 108.61) * mm, "mid": v(-26.74, 105.08) * mm, "end": v(-23.2, 103.61) * mm});
            skLineSegment(sketch, "E293", {"start": v(-23.2, 103.61) * mm, "end": v(-10.28, 103.61) * mm});
            skArc(sketch, "E294", {"start": v(-6.74, 102.15) * mm, "mid": v(-8.36, 103.23) * mm, "end": v(-10.28, 103.61) * mm});
            skLineSegment(sketch, "E295", {"start": v(-6.74, 102.15) * mm, "end": v(0.33, 95.08) * mm});
            skArc(sketch, "E296", {"start": v(0.33, 95.08) * mm, "mid": v(1.95, 94) * mm, "end": v(3.86, 93.61) * mm});
            skLineSegment(sketch, "E297", {"start": v(3.86, 93.61) * mm, "end": v(41.8, 93.61) * mm});
            skArc(sketch, "E298", {"start": v(41.8, 93.61) * mm, "mid": v(45.33, 95.08) * mm, "end": v(46.8, 98.61) * mm});
            skCircle(sketch, "E299", {"center": v(37.3, 100.11) * mm, "radius": 1.6 * mm});
            skCircle(sketch, "E300", {"center": v(6.3, 100.11) * mm, "radius": 1.6 * mm});
            skCircle(sketch, "E301", {"center": v(6.3, 131.11) * mm, "radius": 1.6 * mm});
            skCircle(sketch, "E302", {"center": v(37.3, 131.11) * mm, "radius": 1.6 * mm});
            skCircle(sketch, "E303", {"center": v(-20.2, 113.61) * mm, "radius": 2.1 * mm});
            skCircle(sketch, "E304", {"center": v(-20.2, 133.61) * mm, "radius": 2.1 * mm});
            skCircle(sketch, "E305", {"center": v(-38.2, 133.61) * mm, "radius": 2.1 * mm});
            skCircle(sketch, "E306", {"center": v(21.8, 115.61) * mm, "radius": 11.5 * mm});
            skLineSegment(sketch, "E307", {"start": v(-31.2, -39.22) * mm, "end": v(-24.13, -46.3) * mm});
            skArc(sketch, "E308", {"start": v(-22.67, -49.83) * mm, "mid": v(-23.05, -47.92) * mm, "end": v(-24.13, -46.3) * mm});
            skLineSegment(sketch, "E309", {"start": v(-22.67, -49.83) * mm, "end": v(-22.67, -62.76) * mm});
            skArc(sketch, "E310", {"start": v(-22.67, -62.76) * mm, "mid": v(-21.2, -66.3) * mm, "end": v(-17.67, -67.76) * mm});
            skLineSegment(sketch, "E311", {"start": v(-17.67, -67.76) * mm, "end": v(-7.67, -67.76) * mm});
            skArc(sketch, "E312", {"start": v(-2.67, -72.76) * mm, "mid": v(-4.13, -69.22) * mm, "end": v(-7.67, -67.76) * mm});
            skLineSegment(sketch, "E313", {"start": v(-2.67, -72.76) * mm, "end": v(-2.67, -82.76) * mm});
            skArc(sketch, "E314", {"start": v(-2.67, -82.76) * mm, "mid": v(-1.2, -86.3) * mm, "end": v(2.33, -87.76) * mm});
            skLineSegment(sketch, "E315", {"start": v(2.33, -87.76) * mm, "end": v(12.33, -87.76) * mm});
            skArc(sketch, "E316", {"start": v(12.33, -87.76) * mm, "mid": v(15.87, -86.3) * mm, "end": v(17.33, -82.76) * mm});
            skLineSegment(sketch, "E317", {"start": v(17.33, -82.76) * mm, "end": v(17.33, -12.76) * mm});
            skArc(sketch, "E318", {"start": v(17.33, -12.76) * mm, "mid": v(15.87, -9.22) * mm, "end": v(12.33, -7.76) * mm});
            skLineSegment(sketch, "E319", {"start": v(12.33, -7.76) * mm, "end": v(-27.67, -7.76) * mm});
            skArc(sketch, "E320", {"start": v(-27.67, -7.76) * mm, "mid": v(-31.2, -9.22) * mm, "end": v(-32.67, -12.76) * mm});
            skLineSegment(sketch, "E321", {"start": v(-32.67, -12.76) * mm, "end": v(-32.67, -35.69) * mm});
            skArc(sketch, "E322", {"start": v(-32.67, -35.69) * mm, "mid": v(-32.29, -37.6) * mm, "end": v(-31.2, -39.22) * mm});
            skCircle(sketch, "E323", {"center": v(-10.67, -32.76) * mm, "radius": 2.6 * mm});
            skCircle(sketch, "E324", {"center": v(-25.67, -17.76) * mm, "radius": 2.6 * mm});
            skCircle(sketch, "E325", {"center": v(7.33, -77.76) * mm, "radius": 2.1 * mm});
            skCircle(sketch, "E326", {"center": v(7.33, -49.76) * mm, "radius": 2.1 * mm});
            skCircle(sketch, "E327", {"center": v(-12.67, -49.76) * mm, "radius": 2.1 * mm});
            skLineSegment(sketch, "E328", {"start": v(14.6, 48.58) * mm, "end": v(14.6, 71.07) * mm});
            skArc(sketch, "E329", {"start": v(14.6, 71.07) * mm, "mid": v(13.13, 74.6) * mm, "end": v(9.6, 76.07) * mm});
            skLineSegment(sketch, "E330", {"start": v(9.6, 76.07) * mm, "end": v(-19.7, 76.07) * mm});
            skArc(sketch, "E331", {"start": v(-19.7, 76.07) * mm, "mid": v(-27.72, 74.38) * mm, "end": v(-34.4, 69.62) * mm});
            skLineSegment(sketch, "E332", {"start": v(-34.4, 69.62) * mm, "end": v(-75.64, 24.89) * mm});
            skArc(sketch, "E333", {"start": v(-90.34, 18.44) * mm, "mid": v(-82.31, 20.12) * mm, "end": v(-75.64, 24.89) * mm});
            skLineSegment(sketch, "E334", {"start": v(-90.34, 18.44) * mm, "end": v(-100.47, 18.44) * mm});
            skArc(sketch, "E335", {"start": v(-115.17, 24.89) * mm, "mid": v(-108.5, 20.12) * mm, "end": v(-100.47, 18.44) * mm});
            skLineSegment(sketch, "E336", {"start": v(-115.17, 24.89) * mm, "end": v(-156.4, 69.62) * mm});
            skArc(sketch, "E337", {"start": v(-156.4, 69.62) * mm, "mid": v(-163.09, 74.38) * mm, "end": v(-171.11, 76.07) * mm});
            skLineSegment(sketch, "E338", {"start": v(-171.11, 76.07) * mm, "end": v(-200.4, 76.07) * mm});
            skArc(sketch, "E339", {"start": v(-200.4, 76.07) * mm, "mid": v(-203.94, 74.6) * mm, "end": v(-205.4, 71.07) * mm});
            skLineSegment(sketch, "E340", {"start": v(-205.4, 71.07) * mm, "end": v(-205.4, 48.58) * mm});
            skArc(sketch, "E341", {"start": v(-205.4, 48.58) * mm, "mid": v(-203.72, 40.55) * mm, "end": v(-198.96, 33.87) * mm});
            skLineSegment(sketch, "E342", {"start": v(-198.96, 33.87) * mm, "end": v(-153.63, -7.92) * mm});
            skArc(sketch, "E343", {"start": v(-150.4, -15.27) * mm, "mid": v(-151.24, -11.26) * mm, "end": v(-153.63, -7.92) * mm});
            skLineSegment(sketch, "E344", {"start": v(-150.4, -15.27) * mm, "end": v(-150.4, -52.6) * mm});
            skArc(sketch, "E345", {"start": v(-153.63, -59.95) * mm, "mid": v(-151.24, -56.61) * mm, "end": v(-150.4, -52.6) * mm});
            skLineSegment(sketch, "E346", {"start": v(-153.63, -59.95) * mm, "end": v(-198.96, -101.74) * mm});
            skArc(sketch, "E347", {"start": v(-198.96, -101.74) * mm, "mid": v(-203.72, -108.42) * mm, "end": v(-205.4, -116.44) * mm});
            skLineSegment(sketch, "E348", {"start": v(-205.4, -116.44) * mm, "end": v(-205.4, -138.93) * mm});
            skArc(sketch, "E349", {"start": v(-205.4, -138.93) * mm, "mid": v(-203.94, -142.47) * mm, "end": v(-200.4, -143.93) * mm});
            skLineSegment(sketch, "E350", {"start": v(-200.4, -143.93) * mm, "end": v(-171.11, -143.93) * mm});
            skArc(sketch, "E351", {"start": v(-171.11, -143.93) * mm, "mid": v(-163.09, -142.25) * mm, "end": v(-156.4, -137.49) * mm});
            skLineSegment(sketch, "E352", {"start": v(-156.4, -137.49) * mm, "end": v(-115.17, -92.75) * mm});
            skArc(sketch, "E353", {"start": v(-100.47, -86.3) * mm, "mid": v(-108.5, -88) * mm, "end": v(-115.17, -92.75) * mm});
            skLineSegment(sketch, "E354", {"start": v(-100.47, -86.3) * mm, "end": v(-90.34, -86.3) * mm});
            skArc(sketch, "E355", {"start": v(-75.64, -92.75) * mm, "mid": v(-82.31, -88) * mm, "end": v(-90.34, -86.3) * mm});
            skLineSegment(sketch, "E356", {"start": v(-75.64, -92.75) * mm, "end": v(-34.4, -137.49) * mm});
            skArc(sketch, "E357", {"start": v(-34.4, -137.49) * mm, "mid": v(-27.72, -142.25) * mm, "end": v(-19.7, -143.93) * mm});
            skLineSegment(sketch, "E358", {"start": v(-19.7, -143.93) * mm, "end": v(9.6, -143.93) * mm});
            skArc(sketch, "E359", {"start": v(9.6, -143.93) * mm, "mid": v(13.13, -142.47) * mm, "end": v(14.6, -138.93) * mm});
            skLineSegment(sketch, "E360", {"start": v(14.6, -138.93) * mm, "end": v(14.6, -116.44) * mm});
            skArc(sketch, "E361", {"start": v(14.6, -116.44) * mm, "mid": v(12.91, -108.42) * mm, "end": v(8.15, -101.74) * mm});
            skLineSegment(sketch, "E362", {"start": v(8.15, -101.74) * mm, "end": v(-37.18, -59.95) * mm});
            skArc(sketch, "E363", {"start": v(-40.4, -52.6) * mm, "mid": v(-39.56, -56.61) * mm, "end": v(-37.18, -59.95) * mm});
            skLineSegment(sketch, "E364", {"start": v(-40.4, -52.6) * mm, "end": v(-40.4, -15.27) * mm});
            skArc(sketch, "E365", {"start": v(-37.18, -7.92) * mm, "mid": v(-39.56, -11.26) * mm, "end": v(-40.4, -15.27) * mm});
            skLineSegment(sketch, "E366", {"start": v(-37.18, -7.92) * mm, "end": v(8.15, 33.87) * mm});
            skArc(sketch, "E367", {"start": v(8.15, 33.87) * mm, "mid": v(12.91, 40.55) * mm, "end": v(14.6, 48.58) * mm});
            skCircle(sketch, "E368", {"center": v(-139.85, -13.12) * mm, "radius": 3.56 * mm});
            skCircle(sketch, "E369", {"center": v(-50.96, -13.12) * mm, "radius": 3.56 * mm});
            skCircle(sketch, "E370", {"center": v(-105.4, -43.93) * mm, "radius": 1.52 * mm});
            skCircle(sketch, "E371", {"center": v(-85.4, -43.93) * mm, "radius": 1.52 * mm});
            skCircle(sketch, "E372", {"center": v(-85.4, -23.93) * mm, "radius": 1.52 * mm});
            skCircle(sketch, "E373", {"center": v(-105.4, -23.93) * mm, "radius": 1.52 * mm});
            skCircle(sketch, "E374", {"center": v(9.1, 70.57) * mm, "radius": 1.65 * mm});
            skCircle(sketch, "E375", {"center": v(-199.9, 70.57) * mm, "radius": 1.65 * mm});
            skCircle(sketch, "E376", {"center": v(9.1, -138.43) * mm, "radius": 1.65 * mm});
            skCircle(sketch, "E377", {"center": v(-199.9, -138.43) * mm, "radius": 1.65 * mm});
            skCircle(sketch, "E378", {"center": v(-50.96, -54.74) * mm, "radius": 2.55 * mm});
            skCircle(sketch, "E379", {"center": v(-139.85, -54.74) * mm, "radius": 2.55 * mm});
            skLineSegment(sketch, "E380", {"start": v(-43.4, -38.93) * mm, "end": v(-43.4, -28.93) * mm});
            skLineSegment(sketch, "E381", {"start": v(-43.4, -28.93) * mm, "end": v(-48.4, -28.93) * mm});
            skLineSegment(sketch, "E382", {"start": v(-48.4, -28.93) * mm, "end": v(-48.4, -38.93) * mm});
            skLineSegment(sketch, "E383", {"start": v(-48.4, -38.93) * mm, "end": v(-43.4, -38.93) * mm});
            skLineSegment(sketch, "E384", {"start": v(-142.4, -38.93) * mm, "end": v(-142.4, -28.93) * mm});
            skLineSegment(sketch, "E385", {"start": v(-142.4, -28.93) * mm, "end": v(-147.4, -28.93) * mm});
            skLineSegment(sketch, "E386", {"start": v(-147.4, -28.93) * mm, "end": v(-147.4, -38.93) * mm});
            skLineSegment(sketch, "E387", {"start": v(-147.4, -38.93) * mm, "end": v(-142.4, -38.93) * mm});
            skArc(sketch, "E388", {"start": v(-50.83, -68.97) * mm, "mid": v(-51.22, -67.52) * mm, "end": v(-52.67, -67.13) * mm});
            skLineSegment(sketch, "E389", {"start": v(-52.67, -67.13) * mm, "end": v(-81.11, -74.75) * mm});
            skArc(sketch, "E390", {"start": v(-81.11, -74.75) * mm, "mid": v(-82.17, -75.81) * mm, "end": v(-81.78, -77.26) * mm});
            skLineSegment(sketch, "E391", {"start": v(-81.78, -77.26) * mm, "end": v(-60.96, -98.08) * mm});
            skArc(sketch, "E392", {"start": v(-60.96, -98.08) * mm, "mid": v(-59.51, -98.47) * mm, "end": v(-58.45, -97.41) * mm});
            skLineSegment(sketch, "E393", {"start": v(-58.45, -97.41) * mm, "end": v(-50.83, -68.97) * mm});
            skArc(sketch, "E394", {"start": v(-140.45, 2.08) * mm, "mid": v(-140.06, 0.63) * mm, "end": v(-138.61, 0.25) * mm});
            skLineSegment(sketch, "E395", {"start": v(-138.61, 0.25) * mm, "end": v(-110.17, 7.87) * mm});
            skArc(sketch, "E396", {"start": v(-110.17, 7.87) * mm, "mid": v(-109.1, 8.93) * mm, "end": v(-109.5, 10.38) * mm});
            skLineSegment(sketch, "E397", {"start": v(-109.5, 10.38) * mm, "end": v(-130.32, 31.2) * mm});
            skArc(sketch, "E398", {"start": v(-130.32, 31.2) * mm, "mid": v(-131.77, 31.59) * mm, "end": v(-132.83, 30.53) * mm});
            skLineSegment(sketch, "E399", {"start": v(-132.83, 30.53) * mm, "end": v(-140.45, 2.08) * mm});
            skArc(sketch, "E400", {"start": v(-146.91, -101.5) * mm, "mid": v(-145.46, -101.1) * mm, "end": v(-145.07, -99.66) * mm});
            skLineSegment(sketch, "E401", {"start": v(-145.07, -99.66) * mm, "end": v(-152.7, -71.22) * mm});
            skArc(sketch, "E402", {"start": v(-152.7, -71.22) * mm, "mid": v(-153.76, -70.16) * mm, "end": v(-155.2, -70.54) * mm});
            skLineSegment(sketch, "E403", {"start": v(-155.2, -70.54) * mm, "end": v(-176.03, -91.37) * mm});
            skArc(sketch, "E404", {"start": v(-176.03, -91.37) * mm, "mid": v(-176.41, -92.81) * mm, "end": v(-175.35, -93.87) * mm});
            skLineSegment(sketch, "E405", {"start": v(-175.35, -93.87) * mm, "end": v(-146.91, -101.5) * mm});
            skArc(sketch, "E406", {"start": v(-111.74, -79.51) * mm, "mid": v(-111.36, -78.06) * mm, "end": v(-112.42, -77) * mm});
            skLineSegment(sketch, "E407", {"start": v(-112.42, -77) * mm, "end": v(-140.86, -69.38) * mm});
            skArc(sketch, "E408", {"start": v(-140.86, -69.38) * mm, "mid": v(-142.3, -69.77) * mm, "end": v(-142.7, -71.22) * mm});
            skLineSegment(sketch, "E409", {"start": v(-142.7, -71.22) * mm, "end": v(-135.07, -99.66) * mm});
            skArc(sketch, "E410", {"start": v(-135.07, -99.66) * mm, "mid": v(-134.01, -100.72) * mm, "end": v(-132.56, -100.33) * mm});
            skLineSegment(sketch, "E411", {"start": v(-132.56, -100.33) * mm, "end": v(-111.74, -79.51) * mm});
            skArc(sketch, "E412", {"start": v(-58.2, 28.28) * mm, "mid": v(-59.26, 29.34) * mm, "end": v(-60.7, 28.95) * mm});
            skLineSegment(sketch, "E413", {"start": v(-60.7, 28.95) * mm, "end": v(-81.53, 8.13) * mm});
            skArc(sketch, "E414", {"start": v(-81.53, 8.13) * mm, "mid": v(-81.92, 6.68) * mm, "end": v(-80.86, 5.62) * mm});
            skLineSegment(sketch, "E415", {"start": v(-80.86, 5.62) * mm, "end": v(-52.42, -2) * mm});
            skArc(sketch, "E416", {"start": v(-52.42, -2) * mm, "mid": v(-50.97, -1.61) * mm, "end": v(-50.58, -0.16) * mm});
            skLineSegment(sketch, "E417", {"start": v(-50.58, -0.16) * mm, "end": v(-58.2, 28.28) * mm});
            skArc(sketch, "E418", {"start": v(-22.42, 30.5) * mm, "mid": v(-20.97, 30.89) * mm, "end": v(-20.58, 32.34) * mm});
            skLineSegment(sketch, "E419", {"start": v(-20.58, 32.34) * mm, "end": v(-28.2, 60.78) * mm});
            skArc(sketch, "E420", {"start": v(-28.2, 60.78) * mm, "mid": v(-29.26, 61.84) * mm, "end": v(-30.7, 61.45) * mm});
            skLineSegment(sketch, "E421", {"start": v(-30.7, 61.45) * mm, "end": v(-51.53, 40.63) * mm});
            skArc(sketch, "E422", {"start": v(-51.53, 40.63) * mm, "mid": v(-51.92, 39.18) * mm, "end": v(-50.86, 38.12) * mm});
            skLineSegment(sketch, "E423", {"start": v(-50.86, 38.12) * mm, "end": v(-22.42, 30.5) * mm});
            skArc(sketch, "E424", {"start": v(-142.67, 37.87) * mm, "mid": v(-141.6, 38.93) * mm, "end": v(-142, 40.38) * mm});
            skLineSegment(sketch, "E425", {"start": v(-142, 40.38) * mm, "end": v(-162.82, 61.2) * mm});
            skArc(sketch, "E426", {"start": v(-162.82, 61.2) * mm, "mid": v(-164.27, 61.59) * mm, "end": v(-165.33, 60.53) * mm});
            skLineSegment(sketch, "E427", {"start": v(-165.33, 60.53) * mm, "end": v(-172.95, 32.08) * mm});
            skArc(sketch, "E428", {"start": v(-172.95, 32.08) * mm, "mid": v(-172.56, 30.63) * mm, "end": v(-171.11, 30.25) * mm});
            skLineSegment(sketch, "E429", {"start": v(-171.11, 30.25) * mm, "end": v(-142.67, 37.87) * mm});
            skArc(sketch, "E430", {"start": v(-170.86, -101.88) * mm, "mid": v(-172.3, -102.27) * mm, "end": v(-172.7, -103.72) * mm});
            skLineSegment(sketch, "E431", {"start": v(-172.7, -103.72) * mm, "end": v(-165.07, -132.16) * mm});
            skArc(sketch, "E432", {"start": v(-165.07, -132.16) * mm, "mid": v(-164.01, -133.22) * mm, "end": v(-162.56, -132.83) * mm});
            skLineSegment(sketch, "E433", {"start": v(-162.56, -132.83) * mm, "end": v(-141.74, -112.01) * mm});
            skArc(sketch, "E434", {"start": v(-141.74, -112.01) * mm, "mid": v(-141.36, -110.56) * mm, "end": v(-142.42, -109.5) * mm});
            skLineSegment(sketch, "E435", {"start": v(-142.42, -109.5) * mm, "end": v(-170.86, -101.88) * mm});
            skArc(sketch, "E436", {"start": v(-46.36, 30.12) * mm, "mid": v(-47.81, 29.73) * mm, "end": v(-48.2, 28.28) * mm});
            skLineSegment(sketch, "E437", {"start": v(-48.2, 28.28) * mm, "end": v(-40.58, -0.16) * mm});
            skArc(sketch, "E438", {"start": v(-40.58, -0.16) * mm, "mid": v(-39.52, -1.22) * mm, "end": v(-38.07, -0.84) * mm});
            skLineSegment(sketch, "E439", {"start": v(-38.07, -0.84) * mm, "end": v(-17.25, 19.98) * mm});
            skArc(sketch, "E440", {"start": v(-17.25, 19.98) * mm, "mid": v(-16.86, 21.43) * mm, "end": v(-17.92, 22.5) * mm});
            skLineSegment(sketch, "E441", {"start": v(-17.92, 22.5) * mm, "end": v(-46.36, 30.12) * mm});
            skArc(sketch, "E442", {"start": v(-48.61, -104.75) * mm, "mid": v(-49.67, -105.81) * mm, "end": v(-49.28, -107.26) * mm});
            skLineSegment(sketch, "E443", {"start": v(-49.28, -107.26) * mm, "end": v(-28.46, -128.08) * mm});
            skArc(sketch, "E444", {"start": v(-28.46, -128.08) * mm, "mid": v(-27.01, -128.47) * mm, "end": v(-25.95, -127.41) * mm});
            skLineSegment(sketch, "E445", {"start": v(-25.95, -127.41) * mm, "end": v(-18.33, -98.97) * mm});
            skArc(sketch, "E446", {"start": v(-18.33, -98.97) * mm, "mid": v(-18.72, -97.52) * mm, "end": v(-20.17, -97.13) * mm});
            skLineSegment(sketch, "E447", {"start": v(-20.17, -97.13) * mm, "end": v(-48.61, -104.75) * mm});
            skArc(sketch, "E448", {"start": v(-140.83, 26.03) * mm, "mid": v(-141.22, 27.48) * mm, "end": v(-142.67, 27.87) * mm});
            skLineSegment(sketch, "E449", {"start": v(-142.67, 27.87) * mm, "end": v(-169.7, 20.63) * mm});
            skArc(sketch, "E450", {"start": v(-169.7, 20.63) * mm, "mid": v(-170.75, 19.57) * mm, "end": v(-170.37, 18.12) * mm});
            skLineSegment(sketch, "E451", {"start": v(-170.37, 18.12) * mm, "end": v(-150.58, -1.67) * mm});
            skArc(sketch, "E452", {"start": v(-150.58, -1.67) * mm, "mid": v(-149.13, -2.06) * mm, "end": v(-148.07, -1) * mm});
            skLineSegment(sketch, "E453", {"start": v(-148.07, -1) * mm, "end": v(-140.83, 26.03) * mm});
            skArc(sketch, "E454", {"start": v(-50.45, -92.92) * mm, "mid": v(-50.06, -94.37) * mm, "end": v(-48.61, -94.75) * mm});
            skLineSegment(sketch, "E455", {"start": v(-48.61, -94.75) * mm, "end": v(-21.59, -87.51) * mm});
            skArc(sketch, "E456", {"start": v(-21.59, -87.51) * mm, "mid": v(-20.52, -86.45) * mm, "end": v(-20.91, -85) * mm});
            skLineSegment(sketch, "E457", {"start": v(-20.91, -85) * mm, "end": v(-40.7, -65.22) * mm});
            skArc(sketch, "E458", {"start": v(-40.7, -65.22) * mm, "mid": v(-42.15, -64.83) * mm, "end": v(-43.2, -65.9) * mm});
            skLineSegment(sketch, "E459", {"start": v(-43.2, -65.9) * mm, "end": v(-50.45, -92.92) * mm});
            skArc(sketch, "E460", {"start": v(-123.5, -52.2) * mm, "mid": v(-126, -54.26) * mm, "end": v(-124.45, -57.1) * mm});
            skLineSegment(sketch, "E461", {"start": v(-124.45, -57.1) * mm, "end": v(-96.29, -68.4) * mm});
            skArc(sketch, "E462", {"start": v(-96.29, -68.4) * mm, "mid": v(-95.34, -68.58) * mm, "end": v(-94.4, -68.4) * mm});
            skLineSegment(sketch, "E463", {"start": v(-94.4, -68.4) * mm, "end": v(-66.34, -57.1) * mm});
            skArc(sketch, "E464", {"start": v(-66.34, -57.1) * mm, "mid": v(-64.8, -54.26) * mm, "end": v(-67.28, -52.2) * mm});
            skLineSegment(sketch, "E465", {"start": v(-67.28, -52.2) * mm, "end": v(-123.5, -52.2) * mm});
            skArc(sketch, "E466", {"start": v(-94.77, 0.36) * mm, "mid": v(-95.7, 0.53) * mm, "end": v(-96.63, 0.36) * mm});
            skLineSegment(sketch, "E467", {"start": v(-96.63, 0.36) * mm, "end": v(-124.9, -10.76) * mm});
            skArc(sketch, "E468", {"start": v(-124.9, -10.76) * mm, "mid": v(-126.47, -13.6) * mm, "end": v(-123.98, -15.66) * mm});
            skLineSegment(sketch, "E469", {"start": v(-123.98, -15.66) * mm, "end": v(-67.43, -15.66) * mm});
            skArc(sketch, "E470", {"start": v(-67.43, -15.66) * mm, "mid": v(-64.93, -13.6) * mm, "end": v(-66.5, -10.76) * mm});
            skLineSegment(sketch, "E471", {"start": v(-66.5, -10.76) * mm, "end": v(-94.77, 0.36) * mm});
            skLineSegment(sketch, "E472", {"start": v(-100.55, 44.83) * mm, "end": v(-99.74, 45.64) * mm});
            skArc(sketch, "E473", {"start": v(-96.91, 45.64) * mm, "mid": v(-98.32, 46.23) * mm, "end": v(-99.74, 45.64) * mm});
            skLineSegment(sketch, "E474", {"start": v(-96.91, 45.64) * mm, "end": v(-96.1, 44.83) * mm});
            skArc(sketch, "E475", {"start": v(-96.1, 44.83) * mm, "mid": v(-95.45, 44.4) * mm, "end": v(-94.69, 44.25) * mm});
            skLineSegment(sketch, "E476", {"start": v(-94.69, 44.25) * mm, "end": v(-72.63, 44.25) * mm});
            skArc(sketch, "E477", {"start": v(-72.63, 44.25) * mm, "mid": v(-69.1, 45.7) * mm, "end": v(-67.63, 49.25) * mm});
            skLineSegment(sketch, "E478", {"start": v(-67.63, 49.25) * mm, "end": v(-67.63, 59.35) * mm});
            skArc(sketch, "E479", {"start": v(-64.55, 66.57) * mm, "mid": v(-66.83, 63.27) * mm, "end": v(-67.63, 59.35) * mm});
            skLineSegment(sketch, "E480", {"start": v(-64.55, 66.57) * mm, "end": v(-36.29, 93.66) * mm});
            skArc(sketch, "E481", {"start": v(-36.29, 93.66) * mm, "mid": v(-34, 96.96) * mm, "end": v(-33.2, 100.88) * mm});
            skLineSegment(sketch, "E482", {"start": v(-33.2, 100.88) * mm, "end": v(-33.2, 113.61) * mm});
            skArc(sketch, "E483", {"start": v(-33.2, 113.61) * mm, "mid": v(-34.67, 117.15) * mm, "end": v(-38.2, 118.61) * mm});
            skLineSegment(sketch, "E484", {"start": v(-38.2, 118.61) * mm, "end": v(-62.63, 118.61) * mm});
            skArc(sketch, "E485", {"start": v(-67.63, 123.61) * mm, "mid": v(-66.17, 120.08) * mm, "end": v(-62.63, 118.61) * mm});
            skLineSegment(sketch, "E486", {"start": v(-67.63, 123.61) * mm, "end": v(-67.63, 138.14) * mm});
            skArc(sketch, "E487", {"start": v(-67.63, 138.14) * mm, "mid": v(-69.1, 141.67) * mm, "end": v(-72.63, 143.14) * mm});
            skLineSegment(sketch, "E488", {"start": v(-72.63, 143.14) * mm, "end": v(-124.01, 143.14) * mm});
            skArc(sketch, "E489", {"start": v(-124.01, 143.14) * mm, "mid": v(-127.55, 141.67) * mm, "end": v(-129.01, 138.14) * mm});
            skLineSegment(sketch, "E490", {"start": v(-129.01, 138.14) * mm, "end": v(-129.01, 49.25) * mm});
            skArc(sketch, "E491", {"start": v(-129.01, 49.25) * mm, "mid": v(-127.55, 45.7) * mm, "end": v(-124.01, 44.25) * mm});
            skLineSegment(sketch, "E492", {"start": v(-124.01, 44.25) * mm, "end": v(-101.96, 44.25) * mm});
            skArc(sketch, "E493", {"start": v(-101.96, 44.25) * mm, "mid": v(-101.2, 44.4) * mm, "end": v(-100.55, 44.83) * mm});
            skCircle(sketch, "E494", {"center": v(-77.82, 133.14) * mm, "radius": 3.56 * mm});
            skCircle(sketch, "E495", {"center": v(-119.82, 133.14) * mm, "radius": 2.55 * mm});
            skCircle(sketch, "E496", {"center": v(-77.82, 54.25) * mm, "radius": 3.56 * mm});
            skCircle(sketch, "E497", {"center": v(-119.82, 54.25) * mm, "radius": 2.55 * mm});
            skCircle(sketch, "E498", {"center": v(-114.6, 78.61) * mm, "radius": 2.1 * mm});
            skCircle(sketch, "E499", {"center": v(-83.1, 78.61) * mm, "radius": 2.1 * mm});
            skCircle(sketch, "E500", {"center": v(-41.06, 112.11) * mm, "radius": 2.6 * mm});
            skCircle(sketch, "E501", {"center": v(-56.06, 96.61) * mm, "radius": 2.6 * mm});
            skCircle(sketch, "E502", {"center": v(-83.1, 98.61) * mm, "radius": 2.1 * mm});
            skCircle(sketch, "E503", {"center": v(-114.6, 98.61) * mm, "radius": 2.1 * mm});
            skArc(sketch, "E504", {"start": v(-103.27, 128.78) * mm, "mid": v(-106.86, 127.29) * mm, "end": v(-108.35, 123.7) * mm});
            skLineSegment(sketch, "E505", {"start": v(-108.35, 123.7) * mm, "end": v(-108.35, 64.64) * mm});
            skArc(sketch, "E506", {"start": v(-108.35, 64.64) * mm, "mid": v(-106.86, 61.05) * mm, "end": v(-103.27, 59.56) * mm});
            skLineSegment(sketch, "E507", {"start": v(-103.27, 59.56) * mm, "end": v(-94.38, 59.56) * mm});
            skArc(sketch, "E508", {"start": v(-94.38, 59.56) * mm, "mid": v(-90.79, 61.05) * mm, "end": v(-89.3, 64.64) * mm});
            skLineSegment(sketch, "E509", {"start": v(-89.3, 64.64) * mm, "end": v(-89.3, 123.7) * mm});
            skArc(sketch, "E510", {"start": v(-89.3, 123.7) * mm, "mid": v(-90.79, 127.29) * mm, "end": v(-94.38, 128.78) * mm});
            skLineSegment(sketch, "E511", {"start": v(-94.38, 128.78) * mm, "end": v(-103.27, 128.78) * mm});
            skLineSegment(sketch, "E512", {"start": v(-124.88, -112.22) * mm, "end": v(-124.88, -139.93) * mm});
            skArc(sketch, "E513", {"start": v(-124.88, -139.93) * mm, "mid": v(-123.7, -142.76) * mm, "end": v(-120.88, -143.93) * mm});
            skLineSegment(sketch, "E514", {"start": v(-120.88, -143.93) * mm, "end": v(-86.2, -143.93) * mm});
            skArc(sketch, "E515", {"start": v(-86.2, -143.93) * mm, "mid": v(-81.25, -141.88) * mm, "end": v(-79.2, -136.93) * mm});
            skLineSegment(sketch, "E516", {"start": v(-79.2, -136.93) * mm, "end": v(-79.2, -115.22) * mm});
            skArc(sketch, "E517", {"start": v(-79.2, -115.22) * mm, "mid": v(-81.25, -110.27) * mm, "end": v(-86.2, -108.22) * mm});
            skLineSegment(sketch, "E518", {"start": v(-86.2, -108.22) * mm, "end": v(-120.88, -108.22) * mm});
            skArc(sketch, "E519", {"start": v(-120.88, -108.22) * mm, "mid": v(-123.7, -109.4) * mm, "end": v(-124.88, -112.22) * mm});
            skCircle(sketch, "E520", {"center": v(-90.23, -126) * mm, "radius": 5.26 * mm});
            skCircle(sketch, "E521", {"center": v(-114.83, -115.92) * mm, "radius": 2.12 * mm});
            skCircle(sketch, "E522", {"center": v(-95.92, -120.38) * mm, "radius": 1.75 * mm});
            skCircle(sketch, "E523", {"center": v(-84.66, -120.38) * mm, "radius": 1.75 * mm});
            skCircle(sketch, "E524", {"center": v(-114.83, -136) * mm, "radius": 2.12 * mm});
            skCircle(sketch, "E525", {"center": v(-95.92, -131.53) * mm, "radius": 1.75 * mm});
            skCircle(sketch, "E526", {"center": v(-84.66, -131.53) * mm, "radius": 1.75 * mm});
            skLineSegment(sketch, "E527", {"start": v(-143.4, 81.07) * mm, "end": v(-135.4, 89.07) * mm});
            skLineSegment(sketch, "E528", {"start": v(-135.4, 89.07) * mm, "end": v(-135.4, 135.45) * mm});
            skLineSegment(sketch, "E529", {"start": v(-135.4, 135.45) * mm, "end": v(-143.4, 143.45) * mm});
            skLineSegment(sketch, "E530", {"start": v(-143.4, 143.45) * mm, "end": v(-197.4, 143.45) * mm});
            skLineSegment(sketch, "E531", {"start": v(-197.4, 143.45) * mm, "end": v(-205.4, 135.45) * mm});
            skLineSegment(sketch, "E532", {"start": v(-205.4, 135.45) * mm, "end": v(-205.4, 89.07) * mm});
            skLineSegment(sketch, "E533", {"start": v(-205.4, 89.07) * mm, "end": v(-197.4, 81.07) * mm});
            skLineSegment(sketch, "E534", {"start": v(-197.4, 81.07) * mm, "end": v(-143.4, 81.07) * mm});
            skCircle(sketch, "E535", {"center": v(-160.63, 122.26) * mm, "radius": 1.6 * mm});
            skCircle(sketch, "E536", {"center": v(-180.63, 122.26) * mm, "radius": 1.6 * mm});
            skCircle(sketch, "E537", {"center": v(-180.63, 102.26) * mm, "radius": 1.6 * mm});
            skCircle(sketch, "E538", {"center": v(-160.63, 102.26) * mm, "radius": 1.6 * mm});
            skCircle(sketch, "E539", {"center": v(-170.4, 138.02) * mm, "radius": 1.26 * mm});
            skCircle(sketch, "E540", {"center": v(-155.49, 86.04) * mm, "radius": 1.26 * mm});
            skCircle(sketch, "E541", {"center": v(-185.43, 86.04) * mm, "radius": 1.26 * mm});
            skCircle(sketch, "E542", {"center": v(-140.4, 122.26) * mm, "radius": 1.25 * mm});
            skCircle(sketch, "E543", {"center": v(-142.9, 133.26) * mm, "radius": 3.56 * mm});
            skCircle(sketch, "E544", {"center": v(-193.36, 100.41) * mm, "radius": 1.25 * mm});
            skCircle(sketch, "E545", {"center": v(-201.36, 100.41) * mm, "radius": 1.6 * mm});
            skCircle(sketch, "E546", {"center": v(-197.9, 133.26) * mm, "radius": 3.56 * mm});
            skCircle(sketch, "E547", {"center": v(-197.9, 91.25) * mm, "radius": 2.55 * mm});
            skCircle(sketch, "E548", {"center": v(-142.9, 91.25) * mm, "radius": 2.55 * mm});
            skCircle(sketch, "E549", {"center": v(-140.4, 102.26) * mm, "radius": 1.25 * mm});
            skLineSegment(sketch, "E550", {"start": v(-142.9, 107.26) * mm, "end": v(-137.9, 107.26) * mm});
            skLineSegment(sketch, "E551", {"start": v(-137.9, 107.26) * mm, "end": v(-137.9, 117.26) * mm});
            skLineSegment(sketch, "E552", {"start": v(-137.9, 117.26) * mm, "end": v(-142.9, 117.26) * mm});
            skLineSegment(sketch, "E553", {"start": v(-142.9, 117.26) * mm, "end": v(-142.9, 107.26) * mm});
            skLineSegment(sketch, "E554", {"start": v(-202.9, 107.26) * mm, "end": v(-197.9, 107.26) * mm});
            skLineSegment(sketch, "E555", {"start": v(-197.9, 107.26) * mm, "end": v(-197.9, 117.26) * mm});
            skLineSegment(sketch, "E556", {"start": v(-197.9, 117.26) * mm, "end": v(-202.9, 117.26) * mm});
            skLineSegment(sketch, "E557", {"start": v(-202.9, 117.26) * mm, "end": v(-202.9, 107.26) * mm});
            skArc(sketch, "E558", {"start": v(-169.48, 104.85) * mm, "mid": v(-170.4, 105.25) * mm, "end": v(-171.33, 104.85) * mm});
            skLineSegment(sketch, "E559", {"start": v(-171.33, 104.85) * mm, "end": v(-183.03, 92.46) * mm});
            skLineSegment(sketch, "E560", {"start": v(-183.03, 92.46) * mm, "end": v(-182.4, 91) * mm});
            skLineSegment(sketch, "E561", {"start": v(-182.4, 91) * mm, "end": v(-158.4, 91) * mm});
            skLineSegment(sketch, "E562", {"start": v(-158.4, 91) * mm, "end": v(-157.78, 92.46) * mm});
            skLineSegment(sketch, "E563", {"start": v(-157.78, 92.46) * mm, "end": v(-169.48, 104.85) * mm});
            skLineSegment(sketch, "E564", {"start": v(-169.48, 119.16) * mm, "end": v(-157.78, 131.55) * mm});
            skLineSegment(sketch, "E565", {"start": v(-157.78, 131.55) * mm, "end": v(-158.4, 133) * mm});
            skLineSegment(sketch, "E566", {"start": v(-158.4, 133) * mm, "end": v(-182.4, 133) * mm});
            skLineSegment(sketch, "E567", {"start": v(-182.4, 133) * mm, "end": v(-183.03, 131.55) * mm});
            skLineSegment(sketch, "E568", {"start": v(-183.03, 131.55) * mm, "end": v(-171.33, 119.16) * mm});
            skArc(sketch, "E569", {"start": v(-171.33, 119.16) * mm, "mid": v(-170.4, 118.76) * mm, "end": v(-169.48, 119.16) * mm});
            skLineSegment(sketch, "E570", {"start": v(-150.4, 99) * mm, "end": v(-150.4, 125) * mm});
            skLineSegment(sketch, "E571", {"start": v(-150.4, 125) * mm, "end": v(-151.78, 125.55) * mm});
            skLineSegment(sketch, "E572", {"start": v(-151.78, 125.55) * mm, "end": v(-163.75, 112.88) * mm});
            skArc(sketch, "E573", {"start": v(-163.75, 112.88) * mm, "mid": v(-164.1, 112) * mm, "end": v(-163.75, 111.13) * mm});
            skLineSegment(sketch, "E574", {"start": v(-163.75, 111.13) * mm, "end": v(-151.78, 98.46) * mm});
            skLineSegment(sketch, "E575", {"start": v(-151.78, 98.46) * mm, "end": v(-150.4, 99) * mm});
            skArc(sketch, "E576", {"start": v(-177.06, 111.13) * mm, "mid": v(-176.71, 112) * mm, "end": v(-177.06, 112.88) * mm});
            skLineSegment(sketch, "E577", {"start": v(-177.06, 112.88) * mm, "end": v(-189.03, 125.55) * mm});
            skLineSegment(sketch, "E578", {"start": v(-189.03, 125.55) * mm, "end": v(-190.4, 125) * mm});
            skLineSegment(sketch, "E579", {"start": v(-190.4, 125) * mm, "end": v(-190.4, 99) * mm});
            skLineSegment(sketch, "E580", {"start": v(-190.4, 99) * mm, "end": v(-189.03, 98.46) * mm});
            skLineSegment(sketch, "E581", {"start": v(-189.03, 98.46) * mm, "end": v(-177.06, 111.13) * mm});
            skLineSegment(sketch, "E582", {"start": v(-205.4, -30.99) * mm, "end": v(-205.4, -58.7) * mm});
            skArc(sketch, "E583", {"start": v(-205.4, -58.7) * mm, "mid": v(-204.23, -61.52) * mm, "end": v(-201.4, -62.7) * mm});
            skLineSegment(sketch, "E584", {"start": v(-201.4, -62.7) * mm, "end": v(-166.72, -62.7) * mm});
            skArc(sketch, "E585", {"start": v(-166.72, -62.7) * mm, "mid": v(-161.77, -60.65) * mm, "end": v(-159.72, -55.7) * mm});
            skLineSegment(sketch, "E586", {"start": v(-159.72, -55.7) * mm, "end": v(-159.72, -33.99) * mm});
            skArc(sketch, "E587", {"start": v(-159.72, -33.99) * mm, "mid": v(-161.77, -29.04) * mm, "end": v(-166.72, -26.99) * mm});
            skLineSegment(sketch, "E588", {"start": v(-166.72, -26.99) * mm, "end": v(-201.4, -26.99) * mm});
            skArc(sketch, "E589", {"start": v(-201.4, -26.99) * mm, "mid": v(-204.23, -28.16) * mm, "end": v(-205.4, -30.99) * mm});
            skCircle(sketch, "E590", {"center": v(-170.76, -44.77) * mm, "radius": 5.26 * mm});
            skCircle(sketch, "E591", {"center": v(-195.36, -34.68) * mm, "radius": 2.12 * mm});
            skCircle(sketch, "E592", {"center": v(-176.44, -39.14) * mm, "radius": 1.75 * mm});
            skCircle(sketch, "E593", {"center": v(-165.18, -39.14) * mm, "radius": 1.75 * mm});
            skCircle(sketch, "E594", {"center": v(-195.36, -54.76) * mm, "radius": 2.12 * mm});
            skCircle(sketch, "E595", {"center": v(-176.44, -50.3) * mm, "radius": 1.75 * mm});
            skCircle(sketch, "E596", {"center": v(-165.18, -50.3) * mm, "radius": 1.75 * mm});
            skSolve(sketch);
        }
        {
            var Q0;
            Q0=makeQuery(id+"F0.imprint","IMPRINT",FACE,{"disambiguationData":[TD([[makeQuery(id+"F0.imprint","IMPRINT",EDGE,{"derivedFrom":sQuery(id+"F0.wireOp",EDGE,"E527")}),1.0]])]});
            var Q1;
            Q1=makeQuery(id+"F0.imprint","IMPRINT",FACE,{"disambiguationData":[TD([[makeQuery(id+"F0.imprint","IMPRINT",EDGE,{"derivedFrom":sQuery(id+"F0.wireOp",EDGE,"E328")}),1.0]])]});
            var Q2;
            Q2=makeQuery(id+"F0.imprint","IMPRINT",FACE,{"disambiguationData":[TD([[makeQuery(id+"F0.imprint","IMPRINT",EDGE,{"derivedFrom":sQuery(id+"F0.wireOp",EDGE,"E283")}),1.0]])]});
            var Q3;
            Q3=makeQuery(id+"F0.imprint","IMPRINT",FACE,{"disambiguationData":[TD([[makeQuery(id+"F0.imprint","IMPRINT",EDGE,{"derivedFrom":sQuery(id+"F0.wireOp",EDGE,"E189")}),1.0]])]});
            extrude(context, id + "F1", {"entities" : qUnion([Q0, Q1, Q2, Q3]), "depth" : 3 * mm, "offsetDistance" : 25 * mm});
        }
    });
